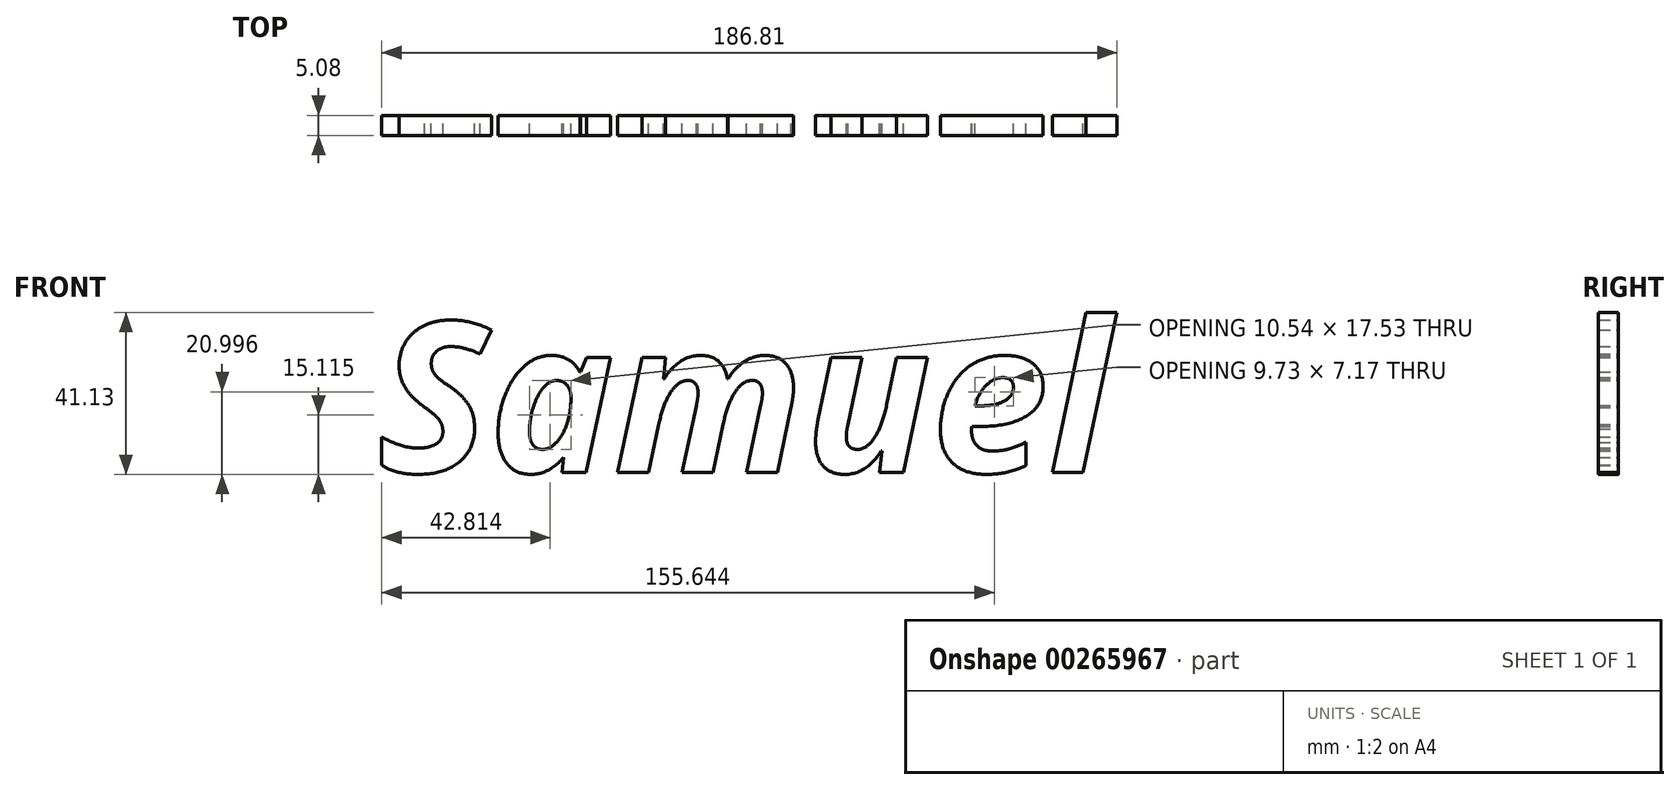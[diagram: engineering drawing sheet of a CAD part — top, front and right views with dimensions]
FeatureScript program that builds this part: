
annotation { "Feature Type Name" : "Feature", "Feature Type Description" : "" }
export const myFeature = defineFeature(function(context is Context, id is Id, definition is map)
    precondition{}
    {
        {
            var Q0;
            Q0=qCreatedBy(makeId("Front.planeOp"),FACE);
            var sketch = newSketch(context, id + "F0", { "sketchPlane" : qUnion([Q0])});
            skText(sketch, "E0", { "text": "Samuel", "fontName": "OpenSans-BoldItalic.ttf"});
            const initialGuessF0  = {"E0": [-0.0658, 0.004, 1, 0, 0.03847]};
            skSetInitialGuess(sketch, initialGuessF0);
            skSolve(sketch);
        }
        {
            var Q0;
            Q0 = qSketchRegion(id + "F0", true);
            extrude(context, id + "F1", {"entities" : qUnion([Q0]), "depth" : 5.08 * mm});
        }
    });
